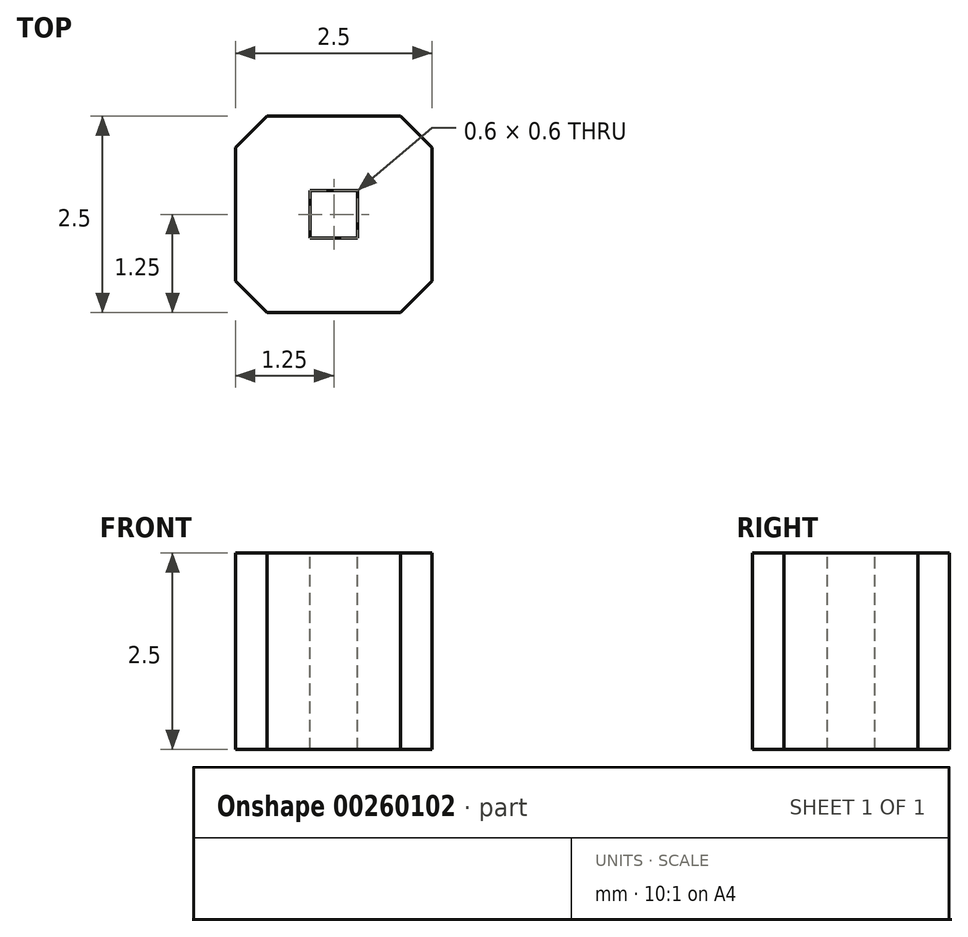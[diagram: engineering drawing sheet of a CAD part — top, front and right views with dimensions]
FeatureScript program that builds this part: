
annotation { "Feature Type Name" : "Feature", "Feature Type Description" : "" }
export const myFeature = defineFeature(function(context is Context, id is Id, definition is map)
    precondition{}
    {
        {
            var Q0;
            Q0=qCreatedBy(makeId("Top.planeOp"),FACE);
            var sketch = newSketch(context, id + "F0", { "sketchPlane" : qUnion([Q0])});
            skLineSegment(sketch, "E0.bottom", {"start": v(0, 0) * mm, "end": v(2.5, 0) * mm});
            skLineSegment(sketch, "E0.top", {"start": v(0, 2.5) * mm, "end": v(2.5, 2.5) * mm});
            skLineSegment(sketch, "E0.left", {"start": v(0, 0) * mm, "end": v(0, 2.5) * mm});
            skLineSegment(sketch, "E0.right", {"start": v(2.5, 0) * mm, "end": v(2.5, 2.5) * mm});
            skSolve(sketch);
        }
        {
            var Q0;
            Q0 = qSketchRegion(id + "F0", true);
            extrude(context, id + "F1", {"entities" : qUnion([Q0]), "depth" : 2.5 * mm});
        }
        {
            var Q0;
            Q0=makeQuery(id+"F1.opExtrude","CAP_FACE",FACE,{"disambiguationData":[OSD([sQuery(id+"F0.wireOp",EDGE,"E0.bottom"),sQuery(id+"F0.wireOp",EDGE,"E0.top"),sQuery(id+"F0.wireOp",EDGE,"E0.left"),sQuery(id+"F0.wireOp",EDGE,"E0.right")])],"isStart":false});
            var sketch = newSketch(context, id + "F2", { "sketchPlane" : qUnion([Q0])});
            skLineSegment(sketch, "E1.bottom", {"start": v(0.95, 1.55) * mm, "end": v(1.55, 1.55) * mm});
            skLineSegment(sketch, "E1.top", {"start": v(0.95, 0.95) * mm, "end": v(1.55, 0.95) * mm});
            skLineSegment(sketch, "E1.left", {"start": v(0.95, 1.55) * mm, "end": v(0.95, 0.95) * mm});
            skLineSegment(sketch, "E1.right", {"start": v(1.55, 1.55) * mm, "end": v(1.55, 0.95) * mm});
            skSolve(sketch);
        }
        {
            var Q0;
            Q0 = qSketchRegion(id + "F2", true);
            extrude(context, id + "F3", {"entities" : qUnion([Q0]), "operationType" : NewBodyOperationType.REMOVE, "oppositeDirection" : true, "depth" : 25 * mm});
        }
        {
            var Q0;
            Q0=makeQuery(id+"F1.opExtrude","SWEPT_EDGE",EDGE,{"disambiguationData":[OSD([sQuery(id+"F0.wireOp",EDGE,"E0.bottom"),sQuery(id+"F0.wireOp",EDGE,"E0.left")])]});
            var Q1;
            Q1=makeQuery(id+"F1.opExtrude","SWEPT_EDGE",EDGE,{"disambiguationData":[OSD([sQuery(id+"F0.wireOp",EDGE,"E0.bottom"),sQuery(id+"F0.wireOp",EDGE,"E0.right")])]});
            var Q2;
            Q2=makeQuery(id+"F1.opExtrude","SWEPT_EDGE",EDGE,{"disambiguationData":[OSD([sQuery(id+"F0.wireOp",EDGE,"E0.top"),sQuery(id+"F0.wireOp",EDGE,"E0.right")])]});
            var Q3;
            Q3=makeQuery(id+"F1.opExtrude","SWEPT_EDGE",EDGE,{"disambiguationData":[OSD([sQuery(id+"F0.wireOp",EDGE,"E0.top"),sQuery(id+"F0.wireOp",EDGE,"E0.left")])]});
            chamfer(context, id + "F4", {"entities" : qUnion([Q0, Q1, Q2, Q3]), "width" : 0.4 * mm, "tangentPropagation" : true});
        }
    });
